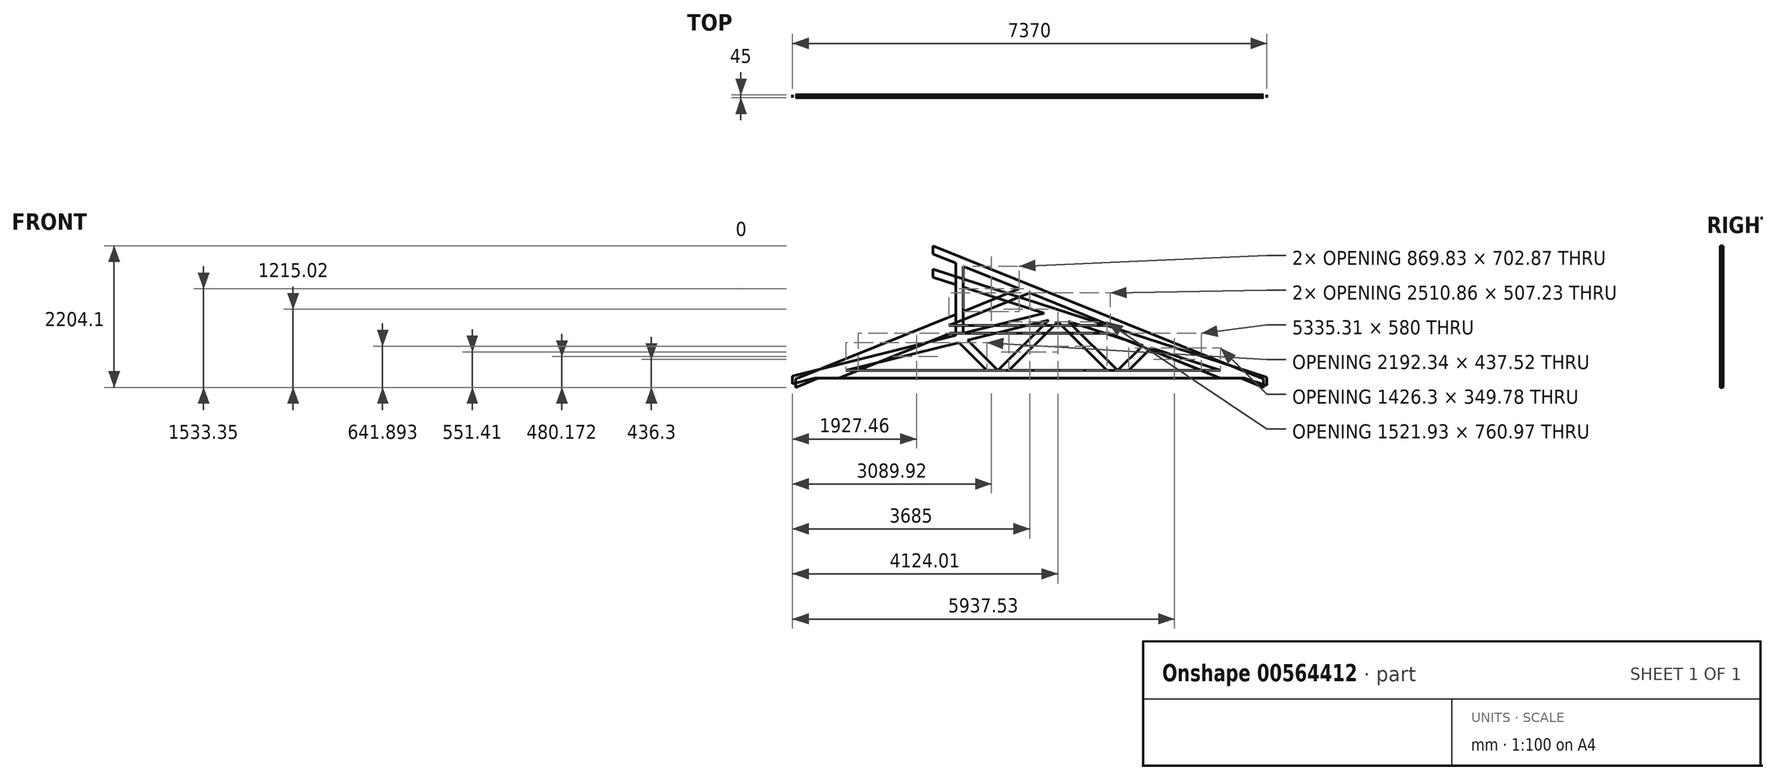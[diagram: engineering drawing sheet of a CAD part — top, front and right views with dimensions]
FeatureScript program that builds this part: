
annotation { "Feature Type Name" : "Feature", "Feature Type Description" : "" }
export const myFeature = defineFeature(function(context is Context, id is Id, definition is map)
    precondition{}
    {
        {
            var Q0;
            Q0=qCreatedBy(makeId("Front.planeOp"),FACE);
            var sketch = newSketch(context, id + "F0", { "sketchPlane" : qUnion([Q0])});
            skLineSegment(sketch, "E0", {"start": v(-3335, 0) * mm, "end": v(3335, 0) * mm});
            skLineSegment(sketch, "E1", {"start": v(-2853.7, 120) * mm, "end": v(2965.68, 120) * mm});
            skLineSegment(sketch, "E2", {"start": v(-3335, 0) * mm, "end": v(439, 940.97) * mm, "construction": true});
            skLineSegment(sketch, "E3", {"start": v(439, 940.97) * mm, "end": v(3335, 0) * mm, "construction": true});
            skLineSegment(sketch, "E4", {"start": v(3685, -113.72) * mm, "end": v(-1500, 1570.99) * mm});
            skLineSegment(sketch, "E5", {"start": v(-1500, 1697.16) * mm, "end": v(3685, 12.45) * mm});
            skLineSegment(sketch, "E6", {"start": v(3685, 12.45) * mm, "end": v(3685, -113.72) * mm});
            skLineSegment(sketch, "E7", {"start": v(439, 940.97) * mm, "end": v(-3685, -87.26) * mm});
            skLineSegment(sketch, "E8", {"start": v(-3685, 36.4) * mm, "end": v(223.64, 1010.94) * mm});
            skLineSegment(sketch, "E9", {"start": v(-3685, -87.26) * mm, "end": v(-3685, 36.4) * mm});
            skLineSegment(sketch, "E10", {"start": v(-1500, 1697.16) * mm, "end": v(-1500, 1570.99) * mm});
            skLineSegment(sketch, "E11", {"start": v(-1150, 1457.26) * mm, "end": v(-1150, 668.46) * mm});
            skLineSegment(sketch, "E12", {"start": v(-1030, 1418.27) * mm, "end": v(-1030, 698.37) * mm});
            skLineSegment(sketch, "E13", {"start": v(439, 940.97) * mm, "end": v(439, 880.97) * mm});
            skLineSegment(sketch, "E14", {"start": v(439, 880.97) * mm, "end": v(-321.96, 120) * mm});
            skLineSegment(sketch, "E15", {"start": v(-491.66, 120) * mm, "end": v(292.86, 904.53) * mm});
            skLineSegment(sketch, "E16", {"start": v(439, 880.97) * mm, "end": v(1199.97, 120) * mm});
            skLineSegment(sketch, "E17", {"start": v(1369.68, 120) * mm, "end": v(601.51, 888.16) * mm});
            skLineSegment(sketch, "E18", {"start": v(-491.66, 120) * mm, "end": v(-963.06, 591.4) * mm});
            skLineSegment(sketch, "E19", {"start": v(-661.37, 120) * mm, "end": v(-1098.9, 557.52) * mm});
            skLineSegment(sketch, "E20", {"start": v(1369.68, 120) * mm, "end": v(1761.08, 511.4) * mm});
            skLineSegment(sketch, "E21", {"start": v(1539.38, 120) * mm, "end": v(1889.16, 469.78) * mm});
            skSolve(sketch);
        }
        {
            var Q0;
            {var subQ5=sQuery(id+"F0.wireOp",EDGE,"E9");Q0=makeQuery(id+"F0.imprint","IMPRINT",FACE,{"disambiguationData":[TD([[makeQuery(id+"F0.imprint","IMPRINT",EDGE,{"derivedFrom":subQ5}),-1.0]])]});}
            var Q1;
            {var subQ0=sQuery(id+"F0.wireOp",EDGE,"E11");Q1=makeQuery(id+"F0.imprint","IMPRINT",FACE,{"disambiguationData":[TD([[makeQuery(id+"F0.imprint","IMPRINT",EDGE,{"derivedFrom":subQ0}),1.0]])]});}
            var Q2;
            Q2=makeQuery(id+"F0.imprint","IMPRINT",FACE,{"disambiguationData":[TD([[makeQuery(id+"F0.imprint","IMPRINT",EDGE,{"derivedFrom":sQuery(id+"F0.wireOp",EDGE,"E5")}),-1.0]])]});
            var Q3;
            {var subQ1=sQuery(id+"F0.wireOp",EDGE,"E13");Q3=makeQuery(id+"F0.imprint","IMPRINT",FACE,{"disambiguationData":[TD([[makeQuery(id+"F0.imprint","IMPRINT",EDGE,{"derivedFrom":subQ1}),1.0]])]});}
            var Q4;
            {var subQ0=sQuery(id+"F0.wireOp",EDGE,"E20");Q4=makeQuery(id+"F0.imprint","IMPRINT",FACE,{"disambiguationData":[TD([[makeQuery(id+"F0.imprint","IMPRINT",EDGE,{"derivedFrom":subQ0}),-1.0]])]});}
            var Q5;
            {var subQ5=sQuery(id+"F0.wireOp",EDGE,"E0");Q5=makeQuery(id+"F0.imprint","IMPRINT",FACE,{"disambiguationData":[TD([[makeQuery(id+"F0.imprint","IMPRINT",EDGE,{"derivedFrom":subQ5}),1.0]])]});}
            var Q6;
            {var subQ1=sQuery(id+"F0.wireOp",EDGE,"E13");Q6=makeQuery(id+"F0.imprint","IMPRINT",FACE,{"disambiguationData":[TD([[makeQuery(id+"F0.imprint","IMPRINT",EDGE,{"derivedFrom":subQ1}),-1.0]])]});}
            var Q7;
            {var subQ0=sQuery(id+"F0.wireOp",EDGE,"E18");Q7=makeQuery(id+"F0.imprint","IMPRINT",FACE,{"disambiguationData":[TD([[makeQuery(id+"F0.imprint","IMPRINT",EDGE,{"derivedFrom":subQ0}),1.0]])]});}
            extrude(context, id + "F1", {"entities" : qUnion([Q0, Q1, Q2, Q3, Q4, Q5, Q6, Q7]), "depth" : 45 * mm, "offsetDistance" : 25 * mm});
        }
        {
            var Q0;
            Q0=qCreatedBy(makeId("Front.planeOp"),FACE);
            var sketch = newSketch(context, id + "F2", { "sketchPlane" : qUnion([Q0])});
            skLineSegment(sketch, "E22", {"start": v(-3285, 0) * mm, "end": v(-2964.66, 0) * mm});
            skLineSegment(sketch, "E23", {"start": v(-3285, 0) * mm, "end": v(0, 1327.23) * mm, "construction": true});
            skLineSegment(sketch, "E24", {"start": v(0, 1327.23) * mm, "end": v(3285, 0) * mm, "construction": true});
            skLineSegment(sketch, "E25", {"start": v(3635, -141.4) * mm, "end": v(-1500, 1933.27) * mm});
            skLineSegment(sketch, "E26", {"start": v(-1500, 2062.69) * mm, "end": v(3635, -11.99) * mm});
            skLineSegment(sketch, "E27", {"start": v(3635, -11.99) * mm, "end": v(3635, -141.4) * mm});
            skLineSegment(sketch, "E28", {"start": v(0, 1327.23) * mm, "end": v(-3635, -141.4) * mm});
            skLineSegment(sketch, "E29", {"start": v(-3635, -11.99) * mm, "end": v(-160.17, 1391.94) * mm});
            skLineSegment(sketch, "E30", {"start": v(-3635, -141.4) * mm, "end": v(-3635, -11.99) * mm});
            skLineSegment(sketch, "E31", {"start": v(-1500, 2062.69) * mm, "end": v(-1500, 1933.27) * mm});
            skLineSegment(sketch, "E32", {"start": v(-1150, 1791.86) * mm, "end": v(-1150, 992.02) * mm});
            skLineSegment(sketch, "E33", {"start": v(-1030, 1743.37) * mm, "end": v(-1030, 1040.5) * mm});
            skLineSegment(sketch, "E34", {"start": v(-1255.43, 820) * mm, "end": v(1255.43, 820) * mm});
            skLineSegment(sketch, "E35", {"start": v(-1552.44, 700) * mm, "end": v(1552.44, 700) * mm});
            skLineSegment(sketch, "E36", {"start": v(-2964.66, 0) * mm, "end": v(-1232.1, 700) * mm});
            skLineSegment(sketch, "E37", {"start": v(2964.66, 0) * mm, "end": v(1232.1, 700) * mm});
            skLineSegment(sketch, "E38.trimOffspring", {"start": v(2964.66, 0) * mm, "end": v(3285, 0) * mm});
            skSolve(sketch);
        }
        {
            var Q0;
            Q0=qCreatedBy(makeId("Front.planeOp"),FACE);
            var sketch = newSketch(context, id + "F3", { "sketchPlane" : qUnion([Q0])});
            skLineSegment(sketch, "E39", {"start": v(-3285, 0) * mm, "end": v(0, 1327.23) * mm, "construction": true});
            skLineSegment(sketch, "E40", {"start": v(0, 1327.23) * mm, "end": v(3285, 0) * mm, "construction": true});
            skLineSegment(sketch, "E41", {"start": v(3635, -141.4) * mm, "end": v(-1500, 1933.27) * mm});
            skLineSegment(sketch, "E42", {"start": v(-1500, 2062.69) * mm, "end": v(3635, -11.99) * mm});
            skLineSegment(sketch, "E43", {"start": v(3635, -11.99) * mm, "end": v(3635, -141.4) * mm});
            skLineSegment(sketch, "E44", {"start": v(0, 1327.23) * mm, "end": v(-3635, -141.4) * mm});
            skLineSegment(sketch, "E45", {"start": v(-3635, -11.99) * mm, "end": v(-160.17, 1391.94) * mm});
            skLineSegment(sketch, "E46", {"start": v(-3635, -141.4) * mm, "end": v(-3635, -11.99) * mm});
            skLineSegment(sketch, "E47", {"start": v(-1500, 2062.69) * mm, "end": v(-1500, 1933.27) * mm});
            skLineSegment(sketch, "E48", {"start": v(-1150, 1791.86) * mm, "end": v(-1150, 992.02) * mm});
            skLineSegment(sketch, "E49", {"start": v(-1030, 1743.37) * mm, "end": v(-1030, 1040.5) * mm});
            skLineSegment(sketch, "E50", {"start": v(-1255.43, 820) * mm, "end": v(1255.43, 820) * mm});
            skLineSegment(sketch, "E51", {"start": v(-1552.44, 700) * mm, "end": v(1552.44, 700) * mm});
            skLineSegment(sketch, "E52", {"start": v(-2667.65, 120) * mm, "end": v(-1232.1, 700) * mm});
            skLineSegment(sketch, "E53", {"start": v(2667.65, 120) * mm, "end": v(1232.1, 700) * mm});
            skLineSegment(sketch, "E54", {"start": v(-2987.99, 120) * mm, "end": v(2987.99, 120) * mm});
            skLineSegment(sketch, "E55", {"start": v(-3285, 0) * mm, "end": v(3285, 0) * mm});
            skSolve(sketch);
        }
        {
            var Q0;
            Q0 = qSketchRegion(id + "F2", true);
            extrude(context, id + "F4", {"entities" : qUnion([Q0]), "depth" : 45 * mm, "offsetDistance" : 25 * mm});
        }
        {
            var Q0;
            Q0 = qSketchRegion(id + "F3", true);
            var Q1;
            {var subQ5=sQuery(id+"F3.wireOp",EDGE,"E52");Q1=makeQuery(id+"F3.imprint","IMPRINT",FACE,{"disambiguationData":[TD([[makeQuery(id+"F3.imprint","IMPRINT",EDGE,{"derivedFrom":subQ5}),1.0]])]});}
            var Q2;
            {var subQ4=sQuery(id+"F3.wireOp",EDGE,"E50");Q2=makeQuery(id+"F3.imprint","IMPRINT",FACE,{"disambiguationData":[TD([[makeQuery(id+"F3.imprint","IMPRINT",EDGE,{"derivedFrom":subQ4}),-1.0]])]});}
            var Q3;
            {var subQ5=sQuery(id+"F3.wireOp",EDGE,"E53");Q3=makeQuery(id+"F3.imprint","IMPRINT",FACE,{"disambiguationData":[TD([[makeQuery(id+"F3.imprint","IMPRINT",EDGE,{"derivedFrom":subQ5}),-1.0]])]});}
            extrude(context, id + "F5", {"entities" : qUnion([Q0, Q1, Q2, Q3]), "depth" : 45 * mm, "offsetDistance" : 25 * mm});
        }
    });
